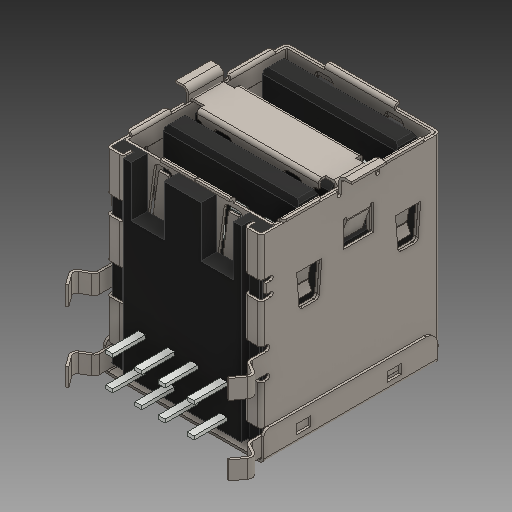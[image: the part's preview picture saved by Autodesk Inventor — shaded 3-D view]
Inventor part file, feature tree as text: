
AUTODESK INVENTOR PART (.ipt)
format: ipt  version: 2018 (Build 220112000, 112)  size: 1,071,616 bytes
history: native  units: mm
features: other x3, sketch x1
ambient origin geometry x8: Origin, YZ Plane, XZ Plane, XY Plane, X Axis, Y Axis, Z Axis, Center Point
bodies: Volumenkörper1 (feature_tree), Volumenkörper2 (feature_tree), Volumenkörper3 (feature_tree), Volumenkörper4 (feature_tree)
feature tree (4):
  sketch  "Sketched Bend22"
  other  "Cut-Extrude5"
  other  "Cut-Extrude8"
  other  "Edge-Flange41"
